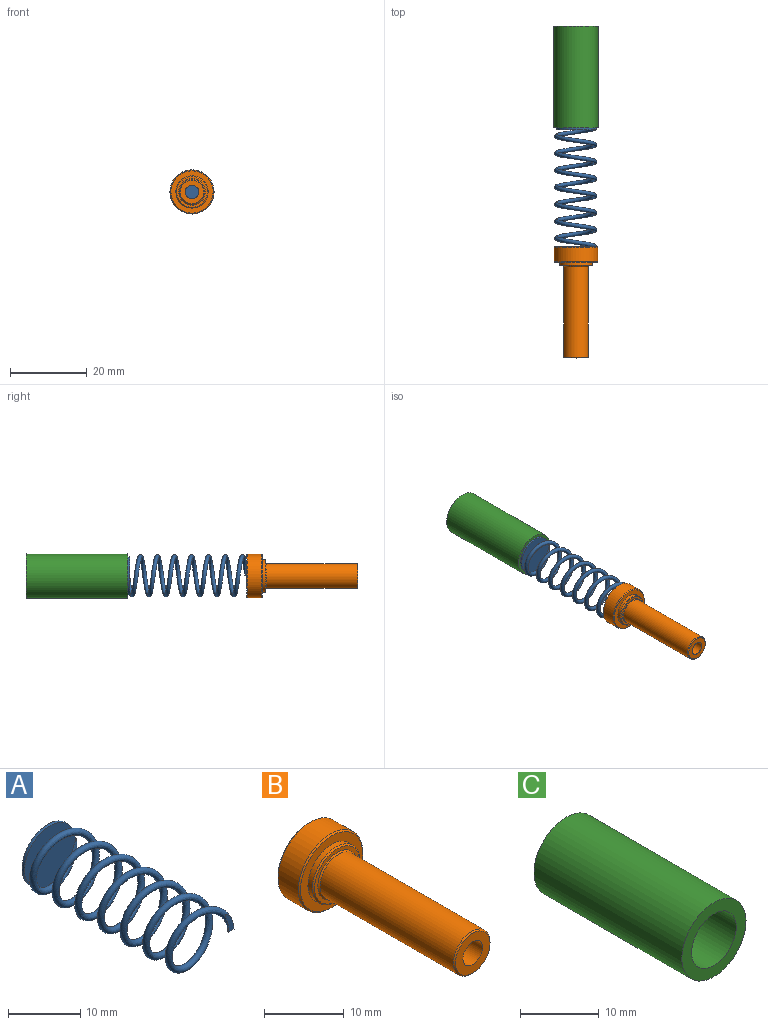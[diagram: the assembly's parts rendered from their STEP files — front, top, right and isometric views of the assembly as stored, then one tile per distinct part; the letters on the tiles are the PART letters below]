
ASSEMBLY  parts=3 mates=2
PART A: 7 faces, bbox 11.3x33.3x13 mm
  f0: bspline ~33x12.7mm, area 683mm2, adj f1,f2,f3,f4,f5,f6
  f1: plane 0.64x0.64mm, normal (0,0,1), area 0.2mm2, adj f0,f3,f5
  f2: plane 1.14x0.64mm, normal (0,0,-1), area 0.4mm2, adj f0,f4
  f3: plane 10.77x10.27mm, normal (0,1,0), area 80mm2, adj f0,f1,f5
  f4: plane 3.25x1.72mm, normal (0,-1,0), area 2.8mm2, adj f0,f2
  f5: cylinder r=5mm len=10mm, axis (0,1,0), area 13mm2, adj f0,f1,f3,f6
  f6: plane 10.31x10.31mm, normal (0,-1,0), area 75.9mm2, adj f0,f5
PART B: 14 faces, bbox 11.4x29x11.4 mm
  f0: cylinder r=3.25mm len=23.6mm, axis (0,1,0), area 481.9mm2, adj f8,f9
  f1: plane 8x8mm, normal (0,-1,0), area 12.9mm2, adj f9,f10
  f2: cylinder r=4.2mm len=8.4mm, axis (0,1,0), area 21.1mm2, adj f3,f10
  f3: plane 11x11mm, normal (0,-1,0), area 39.6mm2, adj f2,f11
  f4: cylinder r=5.7mm len=11.4mm, axis (0,1,0), area 128.9mm2, adj f11,f12
  f5: plane 11x11mm, normal (0,1,0), area 71.3mm2, adj f12,f13
  f6: cylinder r=1.75mm len=28mm, axis (0,1,0), area 307.9mm2, adj f7,f13
  f7: plane 6.1x6.1mm, normal (0,-1,0), area 19.6mm2, adj f6,f8
  f8: cone r=3.25mm half-angle=45deg, axis (0,1,0), area 5.6mm2, adj f0,f7
  f9: cone r=3.45mm half-angle=45deg, axis (0,1,0), area 6mm2, adj f0,f1
  f10: cone r=4.2mm half-angle=45deg, axis (0,1,0), area 7.3mm2, adj f1,f2
  f11: cone r=5.7mm half-angle=45deg, axis (0,1,0), area 10mm2, adj f3,f4
  f12: cone r=5.5mm half-angle=45deg, axis (0,-1,0), area 10mm2, adj f4,f5
  f13: cone r=1.75mm half-angle=45deg, axis (0,1,0), area 20mm2, adj f5,f6
PART C: 4 faces, bbox 11.5x26.5x11.5 mm
  f0: cylinder r=4mm len=26.5mm, axis (0,1,0), area 666mm2, adj f2,f3
  f1: cylinder r=5.75mm len=26.5mm, axis (0,1,0), area 957.4mm2, adj f2,f3
  f2: plane 11.5x11.5mm, normal (0,-1,0), area 53.6mm2, adj f0,f1
  f3: plane 11.5x11.5mm, normal (0,1,0), area 53.6mm2, adj f0,f1
PLACE A t=(-5.54,-21,-2)mm
PLACE B t=(-5.45,-52,-2.03)mm
PLACE C t=(-5.45,5.5,-2.03)mm fixed
MATE fastened C.f1 <-> B.f0  axis (0,-1,0) through (-5.45,-21,-2.03)mm
MATE fastened C.f1 <-> A.f3  axis (0,-1,0) through (-5.45,-21,-2.03)mm
